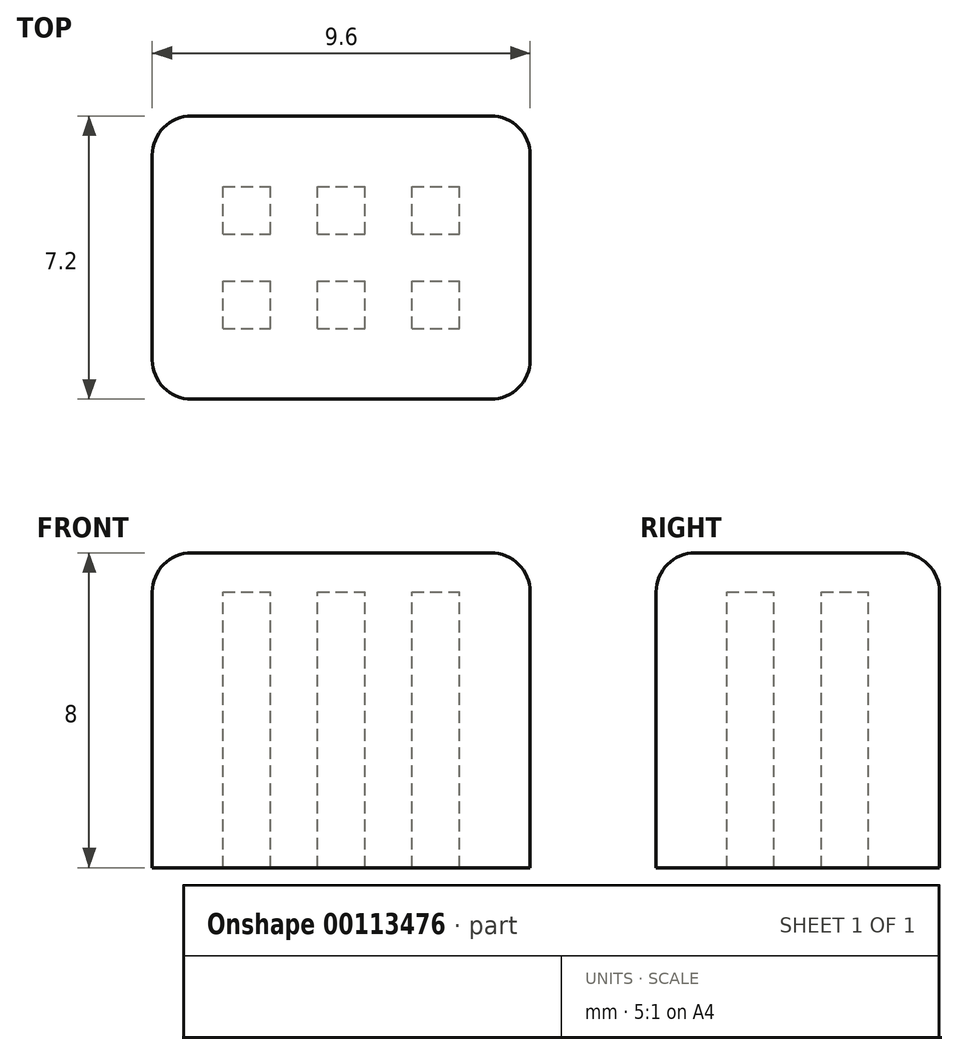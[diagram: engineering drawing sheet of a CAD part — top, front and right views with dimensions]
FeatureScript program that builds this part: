
annotation { "Feature Type Name" : "Feature", "Feature Type Description" : "" }
export const myFeature = defineFeature(function(context is Context, id is Id, definition is map)
    precondition{}
    {
        {
            var Q0;
            Q0=qCreatedBy(makeId("Top.planeOp"),FACE);
            var sketch = newSketch(context, id + "F0", { "sketchPlane" : qUnion([Q0])});
            skLineSegment(sketch, "E0.bottom", {"start": v(0, 0) * mm, "end": v(2.4, 0) * mm});
            skLineSegment(sketch, "E0.top", {"start": v(0, 2.4) * mm, "end": v(2.4, 2.4) * mm});
            skLineSegment(sketch, "E0.left", {"start": v(0, 0) * mm, "end": v(0, 2.4) * mm});
            skLineSegment(sketch, "E0.right", {"start": v(2.4, 0) * mm, "end": v(2.4, 2.4) * mm});
            skLineSegment(sketch, "E1.bottom", {"start": v(0.6, 0.6) * mm, "end": v(1.8, 0.6) * mm});
            skLineSegment(sketch, "E1.top", {"start": v(0.6, 1.8) * mm, "end": v(1.8, 1.8) * mm});
            skLineSegment(sketch, "E1.left", {"start": v(0.6, 0.6) * mm, "end": v(0.6, 1.8) * mm});
            skLineSegment(sketch, "E1.right", {"start": v(1.8, 0.6) * mm, "end": v(1.8, 1.8) * mm});
            skLineSegment(sketch, "E2", {"start": v(1.2, 1.8) * mm, "end": v(1.2, 2.4) * mm, "construction": true});
            skLineSegment(sketch, "E3", {"start": v(0, 1.2) * mm, "end": v(0.6, 1.2) * mm, "construction": true});
            skLineSegment(sketch, "E4.0.1.0", {"start": v(0, 3.6) * mm, "end": v(0.6, 3.6) * mm, "construction": true});
            skLineSegment(sketch, "E4.0.1.1", {"start": v(0, 4.8) * mm, "end": v(2.4, 4.8) * mm});
            skLineSegment(sketch, "E4.0.1.2", {"start": v(2.4, 2.4) * mm, "end": v(2.4, 4.8) * mm});
            skLineSegment(sketch, "E4.0.1.3", {"start": v(1.8, 3) * mm, "end": v(1.8, 4.2) * mm});
            skLineSegment(sketch, "E4.0.1.4", {"start": v(1.2, 4.2) * mm, "end": v(1.2, 4.8) * mm, "construction": true});
            skLineSegment(sketch, "E4.0.1.5", {"start": v(0, 2.4) * mm, "end": v(0, 4.8) * mm});
            skLineSegment(sketch, "E4.0.1.6", {"start": v(0.6, 3) * mm, "end": v(1.8, 3) * mm});
            skLineSegment(sketch, "E4.0.1.7", {"start": v(0.6, 3) * mm, "end": v(0.6, 4.2) * mm});
            skLineSegment(sketch, "E4.0.1.8", {"start": v(0.6, 4.2) * mm, "end": v(1.8, 4.2) * mm});
            skLineSegment(sketch, "E4.1.0.0", {"start": v(2.4, 1.2) * mm, "end": v(3, 1.2) * mm, "construction": true});
            skLineSegment(sketch, "E4.1.0.1", {"start": v(2.4, 2.4) * mm, "end": v(4.8, 2.4) * mm});
            skLineSegment(sketch, "E4.1.0.2", {"start": v(4.8, 0) * mm, "end": v(4.8, 2.4) * mm});
            skLineSegment(sketch, "E4.1.0.3", {"start": v(4.2, 0.6) * mm, "end": v(4.2, 1.8) * mm});
            skLineSegment(sketch, "E4.1.0.4", {"start": v(3.6, 1.8) * mm, "end": v(3.6, 2.4) * mm, "construction": true});
            skLineSegment(sketch, "E4.1.0.6", {"start": v(3, 0.6) * mm, "end": v(4.2, 0.6) * mm});
            skLineSegment(sketch, "E4.1.0.7", {"start": v(3, 0.6) * mm, "end": v(3, 1.8) * mm});
            skLineSegment(sketch, "E4.1.0.8", {"start": v(3, 1.8) * mm, "end": v(4.2, 1.8) * mm});
            skLineSegment(sketch, "E4.1.0.9", {"start": v(2.4, 0) * mm, "end": v(4.8, 0) * mm});
            skLineSegment(sketch, "E4.1.1.0", {"start": v(2.4, 3.6) * mm, "end": v(3, 3.6) * mm, "construction": true});
            skLineSegment(sketch, "E4.1.1.1", {"start": v(2.4, 4.8) * mm, "end": v(4.8, 4.8) * mm});
            skLineSegment(sketch, "E4.1.1.2", {"start": v(4.8, 2.4) * mm, "end": v(4.8, 4.8) * mm});
            skLineSegment(sketch, "E4.1.1.3", {"start": v(4.2, 3) * mm, "end": v(4.2, 4.2) * mm});
            skLineSegment(sketch, "E4.1.1.4", {"start": v(3.6, 4.2) * mm, "end": v(3.6, 4.8) * mm, "construction": true});
            skLineSegment(sketch, "E4.1.1.5", {"start": v(2.4, 2.4) * mm, "end": v(2.4, 4.8) * mm});
            skLineSegment(sketch, "E4.1.1.6", {"start": v(3, 3) * mm, "end": v(4.2, 3) * mm});
            skLineSegment(sketch, "E4.1.1.7", {"start": v(3, 3) * mm, "end": v(3, 4.2) * mm});
            skLineSegment(sketch, "E4.1.1.8", {"start": v(3, 4.2) * mm, "end": v(4.2, 4.2) * mm});
            skLineSegment(sketch, "E4.1.1.9", {"start": v(2.4, 2.4) * mm, "end": v(4.8, 2.4) * mm});
            skLineSegment(sketch, "E4.2.0.0", {"start": v(4.8, 1.2) * mm, "end": v(5.4, 1.2) * mm, "construction": true});
            skLineSegment(sketch, "E4.2.0.1", {"start": v(4.8, 2.4) * mm, "end": v(7.2, 2.4) * mm});
            skLineSegment(sketch, "E4.2.0.2", {"start": v(7.2, 0) * mm, "end": v(7.2, 2.4) * mm});
            skLineSegment(sketch, "E4.2.0.3", {"start": v(6.6, 0.6) * mm, "end": v(6.6, 1.8) * mm});
            skLineSegment(sketch, "E4.2.0.4", {"start": v(6, 1.8) * mm, "end": v(6, 2.4) * mm, "construction": true});
            skLineSegment(sketch, "E4.2.0.5", {"start": v(4.8, 0) * mm, "end": v(4.8, 2.4) * mm});
            skLineSegment(sketch, "E4.2.0.6", {"start": v(5.4, 0.6) * mm, "end": v(6.6, 0.6) * mm});
            skLineSegment(sketch, "E4.2.0.7", {"start": v(5.4, 0.6) * mm, "end": v(5.4, 1.8) * mm});
            skLineSegment(sketch, "E4.2.0.8", {"start": v(5.4, 1.8) * mm, "end": v(6.6, 1.8) * mm});
            skLineSegment(sketch, "E4.2.0.9", {"start": v(4.8, 0) * mm, "end": v(7.2, 0) * mm});
            skLineSegment(sketch, "E4.2.1.0", {"start": v(4.8, 3.6) * mm, "end": v(5.4, 3.6) * mm, "construction": true});
            skLineSegment(sketch, "E4.2.1.1", {"start": v(4.8, 4.8) * mm, "end": v(7.2, 4.8) * mm});
            skLineSegment(sketch, "E4.2.1.2", {"start": v(7.2, 2.4) * mm, "end": v(7.2, 4.8) * mm});
            skLineSegment(sketch, "E4.2.1.3", {"start": v(6.6, 3) * mm, "end": v(6.6, 4.2) * mm});
            skLineSegment(sketch, "E4.2.1.4", {"start": v(6, 4.2) * mm, "end": v(6, 4.8) * mm, "construction": true});
            skLineSegment(sketch, "E4.2.1.5", {"start": v(4.8, 2.4) * mm, "end": v(4.8, 4.8) * mm});
            skLineSegment(sketch, "E4.2.1.6", {"start": v(5.4, 3) * mm, "end": v(6.6, 3) * mm});
            skLineSegment(sketch, "E4.2.1.7", {"start": v(5.4, 3) * mm, "end": v(5.4, 4.2) * mm});
            skLineSegment(sketch, "E4.2.1.8", {"start": v(5.4, 4.2) * mm, "end": v(6.6, 4.2) * mm});
            skLineSegment(sketch, "E4.2.1.9", {"start": v(4.8, 2.4) * mm, "end": v(7.2, 2.4) * mm});
            skLineSegment(sketch, "E4.direction1", {"start": v(0, 0) * mm, "end": v(2.4, 0) * mm, "construction": true});
            skLineSegment(sketch, "E4.direction2", {"start": v(0, 0) * mm, "end": v(0, 2.4) * mm, "construction": true});
            skLineSegment(sketch, "E5.0", {"start": v(-1.2, 2.4) * mm, "end": v(-1.2, 6) * mm});
            skLineSegment(sketch, "E5.1", {"start": v(-1.2, -1.2) * mm, "end": v(-1.2, 2.4) * mm});
            skLineSegment(sketch, "E5.2", {"start": v(-1.2, 6) * mm, "end": v(2.4, 6) * mm});
            skLineSegment(sketch, "E5.3", {"start": v(-1.2, -1.2) * mm, "end": v(2.4, -1.2) * mm});
            skLineSegment(sketch, "E5.4", {"start": v(2.4, -1.2) * mm, "end": v(4.8, -1.2) * mm});
            skLineSegment(sketch, "E5.5", {"start": v(4.8, -1.2) * mm, "end": v(8.4, -1.2) * mm});
            skLineSegment(sketch, "E5.6", {"start": v(2.4, 6) * mm, "end": v(4.8, 6) * mm});
            skLineSegment(sketch, "E5.7", {"start": v(4.8, 6) * mm, "end": v(8.4, 6) * mm});
            skLineSegment(sketch, "E5.8", {"start": v(8.4, 2.4) * mm, "end": v(8.4, 6) * mm});
            skLineSegment(sketch, "E5.9", {"start": v(8.4, -1.2) * mm, "end": v(8.4, 2.4) * mm});
            skSolve(sketch);
        }
        {
            var Q0;
            Q0 = qSketchRegion(id + "F0", true);
            var Q1;
            Q1=makeQuery(id+"F0.imprint","IMPRINT",FACE,{"disambiguationData":[TD([[makeQuery(id+"F0.imprint","IMPRINT",EDGE,{"derivedFrom":sQuery(id+"F0.wireOp",EDGE,"b262808e-0304-4559-aea2-205f56d76e43.0.1.0")}),-1.0]])]});
            var Q2;
            {var subQ0=sQuery(id+"F0.wireOp",EDGE,"rw9Zj4h6-CSxw-FYrh-HEQo-mKNTmKfgoEyw.bottom");Q2=makeQuery(id+"F0.imprint","IMPRINT",FACE,{"disambiguationData":[TD([[makeQuery(id+"F0.imprint","IMPRINT",EDGE,{"derivedFrom":subQ0}),1.0]])]});}
            var Q3;
            Q3=makeQuery(id+"F0.imprint","IMPRINT",FACE,{"disambiguationData":[TD([[makeQuery(id+"F0.imprint","IMPRINT",EDGE,{"derivedFrom":sQuery(id+"F0.wireOp",EDGE,"b262808e-0304-4559-aea2-205f56d76e43.1.0.1")}),1.0]])]});
            var Q4;
            Q4=makeQuery(id+"F0.imprint","IMPRINT",FACE,{"disambiguationData":[TD([[makeQuery(id+"F0.imprint","IMPRINT",EDGE,{"derivedFrom":sQuery(id+"F0.wireOp",EDGE,"b262808e-0304-4559-aea2-205f56d76e43.2.1.0")}),-1.0]])]});
            var Q5;
            Q5=makeQuery(id+"F0.imprint","IMPRINT",FACE,{"disambiguationData":[TD([[makeQuery(id+"F0.imprint","IMPRINT",EDGE,{"derivedFrom":sQuery(id+"F0.wireOp",EDGE,"b262808e-0304-4559-aea2-205f56d76e43.1.1.0")}),-1.0]])]});
            var Q6;
            Q6=makeQuery(id+"F0.imprint","IMPRINT",FACE,{"disambiguationData":[TD([[makeQuery(id+"F0.imprint","IMPRINT",EDGE,{"derivedFrom":sQuery(id+"F0.wireOp",EDGE,"b262808e-0304-4559-aea2-205f56d76e43.2.0.1")}),1.0]])]});
            var Q7;
            Q7=makeQuery(id+"F0.imprint","IMPRINT",FACE,{"disambiguationData":[TD([[makeQuery(id+"F0.imprint","IMPRINT",EDGE,{"derivedFrom":sQuery(id+"F0.wireOp",EDGE,"E4.0.1.1")}),-1.0]])]});
            var Q8;
            Q8=makeQuery(id+"F0.imprint","IMPRINT",FACE,{"disambiguationData":[TD([[makeQuery(id+"F0.imprint","IMPRINT",EDGE,{"derivedFrom":sQuery(id+"F0.wireOp",EDGE,"E4.1.1.1")}),-1.0]])]});
            var Q9;
            Q9=makeQuery(id+"F0.imprint","IMPRINT",FACE,{"disambiguationData":[TD([[makeQuery(id+"F0.imprint","IMPRINT",EDGE,{"derivedFrom":sQuery(id+"F0.wireOp",EDGE,"E4.2.1.1")}),-1.0]])]});
            var Q10;
            Q10=makeQuery(id+"F0.imprint","IMPRINT",FACE,{"disambiguationData":[TD([[makeQuery(id+"F0.imprint","IMPRINT",EDGE,{"derivedFrom":sQuery(id+"F0.wireOp",EDGE,"E4.2.0.2")}),1.0]])]});
            var Q11;
            Q11=makeQuery(id+"F0.imprint","IMPRINT",FACE,{"disambiguationData":[TD([[makeQuery(id+"F0.imprint","IMPRINT",EDGE,{"derivedFrom":sQuery(id+"F0.wireOp",EDGE,"E4.1.0.3")}),-1.0]])]});
            var Q12;
            Q12=makeQuery(id+"F0.imprint","IMPRINT",FACE,{"disambiguationData":[TD([[makeQuery(id+"F0.imprint","IMPRINT",EDGE,{"derivedFrom":sQuery(id+"F0.wireOp",EDGE,"E0.bottom")}),1.0]])]});
            extrude(context, id + "F1", {"entities" : qUnion([Q0, Q1, Q2, Q3, Q4, Q5, Q6, Q7, Q8, Q9, Q10, Q11, Q12]), "oppositeDirection" : true, "depth" : 7 * mm});
        }
        {
            var Q0;
            Q0=makeQuery(id+"F0.imprint","IMPRINT",FACE,{"disambiguationData":[TD([[makeQuery(id+"F0.imprint","IMPRINT",EDGE,{"derivedFrom":sQuery(id+"F0.wireOp",EDGE,"rw9Zj4h6-CSxw-FYrh-HEQo-mKNTmKfgoEyw.bottom")}),1.0]])]});
            var Q1;
            Q1=makeQuery(id+"F0.imprint","IMPRINT",FACE,{"disambiguationData":[TD([[makeQuery(id+"F0.imprint","IMPRINT",EDGE,{"derivedFrom":sQuery(id+"F0.wireOp",EDGE,"JQ0vZeJZ-ZWkE-5OqH-aotH-A3nAdsIy9p33.bottom")}),1.0]])]});
            var Q2;
            {var subQ0=sQuery(id+"F0.wireOp",EDGE,"rw9Zj4h6-CSxw-FYrh-HEQo-mKNTmKfgoEyw.bottom");Q2=makeQuery(id+"F0.imprint","IMPRINT",FACE,{"disambiguationData":[TD([[makeQuery(id+"F0.imprint","IMPRINT",EDGE,{"derivedFrom":subQ0}),-1.0]])]});}
            var Q3;
            Q3=makeQuery(id+"F0.imprint","IMPRINT",FACE,{"disambiguationData":[TD([[makeQuery(id+"F0.imprint","IMPRINT",EDGE,{"derivedFrom":sQuery(id+"F0.wireOp",EDGE,"b262808e-0304-4559-aea2-205f56d76e43.0.1.0")}),-1.0]])]});
            var Q4;
            Q4=makeQuery(id+"F0.imprint","IMPRINT",FACE,{"disambiguationData":[TD([[makeQuery(id+"F0.imprint","IMPRINT",EDGE,{"derivedFrom":sQuery(id+"F0.wireOp",EDGE,"b262808e-0304-4559-aea2-205f56d76e43.0.1.1")}),-1.0]])]});
            var Q5;
            Q5=makeQuery(id+"F0.imprint","IMPRINT",FACE,{"disambiguationData":[TD([[makeQuery(id+"F0.imprint","IMPRINT",EDGE,{"derivedFrom":sQuery(id+"F0.wireOp",EDGE,"b262808e-0304-4559-aea2-205f56d76e43.1.1.1")}),-1.0]])]});
            var Q6;
            Q6=makeQuery(id+"F0.imprint","IMPRINT",FACE,{"disambiguationData":[TD([[makeQuery(id+"F0.imprint","IMPRINT",EDGE,{"derivedFrom":sQuery(id+"F0.wireOp",EDGE,"b262808e-0304-4559-aea2-205f56d76e43.1.1.0")}),-1.0]])]});
            var Q7;
            Q7=makeQuery(id+"F0.imprint","IMPRINT",FACE,{"disambiguationData":[TD([[makeQuery(id+"F0.imprint","IMPRINT",EDGE,{"derivedFrom":sQuery(id+"F0.wireOp",EDGE,"JQ0vZeJZ-ZWkE-5OqH-aotH-A3nAdsIy9p33.top")}),-1.0]])]});
            var Q8;
            Q8=makeQuery(id+"F0.imprint","IMPRINT",FACE,{"disambiguationData":[TD([[makeQuery(id+"F0.imprint","IMPRINT",EDGE,{"derivedFrom":sQuery(id+"F0.wireOp",EDGE,"b262808e-0304-4559-aea2-205f56d76e43.1.0.1")}),-1.0]])]});
            var Q9;
            Q9=makeQuery(id+"F0.imprint","IMPRINT",FACE,{"disambiguationData":[TD([[makeQuery(id+"F0.imprint","IMPRINT",EDGE,{"derivedFrom":sQuery(id+"F0.wireOp",EDGE,"b262808e-0304-4559-aea2-205f56d76e43.2.0.1")}),-1.0]])]});
            var Q10;
            Q10=makeQuery(id+"F0.imprint","IMPRINT",FACE,{"disambiguationData":[TD([[makeQuery(id+"F0.imprint","IMPRINT",EDGE,{"derivedFrom":sQuery(id+"F0.wireOp",EDGE,"b262808e-0304-4559-aea2-205f56d76e43.2.1.1")}),-1.0]])]});
            var Q11;
            Q11=makeQuery(id+"F0.imprint","IMPRINT",FACE,{"disambiguationData":[TD([[makeQuery(id+"F0.imprint","IMPRINT",EDGE,{"derivedFrom":sQuery(id+"F0.wireOp",EDGE,"b262808e-0304-4559-aea2-205f56d76e43.2.1.0")}),-1.0]])]});
            var Q12;
            Q12=makeQuery(id+"F0.imprint","IMPRINT",FACE,{"disambiguationData":[TD([[makeQuery(id+"F0.imprint","IMPRINT",EDGE,{"derivedFrom":sQuery(id+"F0.wireOp",EDGE,"b262808e-0304-4559-aea2-205f56d76e43.2.0.1")}),1.0]])]});
            var Q13;
            Q13=makeQuery(id+"F0.imprint","IMPRINT",FACE,{"disambiguationData":[TD([[makeQuery(id+"F0.imprint","IMPRINT",EDGE,{"derivedFrom":sQuery(id+"F0.wireOp",EDGE,"b262808e-0304-4559-aea2-205f56d76e43.1.0.1")}),1.0]])]});
            var Q14;
            Q14=makeQuery(id+"F0.imprint","IMPRINT",FACE,{"disambiguationData":[TD([[makeQuery(id+"F0.imprint","IMPRINT",EDGE,{"derivedFrom":sQuery(id+"F0.wireOp",EDGE,"E0.bottom")}),-1.0]])]});
            var Q15;
            Q15=makeQuery(id+"F0.imprint","IMPRINT",FACE,{"disambiguationData":[TD([[makeQuery(id+"F0.imprint","IMPRINT",EDGE,{"derivedFrom":sQuery(id+"F0.wireOp",EDGE,"E4.1.1.1")}),-1.0]])]});
            var Q16;
            Q16=makeQuery(id+"F0.imprint","IMPRINT",FACE,{"disambiguationData":[TD([[makeQuery(id+"F0.imprint","IMPRINT",EDGE,{"derivedFrom":sQuery(id+"F0.wireOp",EDGE,"E4.2.1.3")}),1.0]])]});
            var Q17;
            Q17=makeQuery(id+"F0.imprint","IMPRINT",FACE,{"disambiguationData":[TD([[makeQuery(id+"F0.imprint","IMPRINT",EDGE,{"derivedFrom":sQuery(id+"F0.wireOp",EDGE,"E4.2.1.1")}),-1.0]])]});
            var Q18;
            Q18=makeQuery(id+"F0.imprint","IMPRINT",FACE,{"disambiguationData":[TD([[makeQuery(id+"F0.imprint","IMPRINT",EDGE,{"derivedFrom":sQuery(id+"F0.wireOp",EDGE,"E4.1.1.3")}),1.0]])]});
            var Q19;
            Q19=makeQuery(id+"F0.imprint","IMPRINT",FACE,{"disambiguationData":[TD([[makeQuery(id+"F0.imprint","IMPRINT",EDGE,{"derivedFrom":sQuery(id+"F0.wireOp",EDGE,"E4.0.1.3")}),1.0]])]});
            var Q20;
            Q20=makeQuery(id+"F0.imprint","IMPRINT",FACE,{"disambiguationData":[TD([[makeQuery(id+"F0.imprint","IMPRINT",EDGE,{"derivedFrom":sQuery(id+"F0.wireOp",EDGE,"E4.0.1.1")}),-1.0]])]});
            var Q21;
            Q21=makeQuery(id+"F0.imprint","IMPRINT",FACE,{"disambiguationData":[TD([[makeQuery(id+"F0.imprint","IMPRINT",EDGE,{"derivedFrom":sQuery(id+"F0.wireOp",EDGE,"E0.bottom")}),1.0]])]});
            var Q22;
            Q22=makeQuery(id+"F0.imprint","IMPRINT",FACE,{"disambiguationData":[TD([[makeQuery(id+"F0.imprint","IMPRINT",EDGE,{"derivedFrom":sQuery(id+"F0.wireOp",EDGE,"E1.bottom")}),1.0]])]});
            var Q23;
            Q23=makeQuery(id+"F0.imprint","IMPRINT",FACE,{"disambiguationData":[TD([[makeQuery(id+"F0.imprint","IMPRINT",EDGE,{"derivedFrom":sQuery(id+"F0.wireOp",EDGE,"E4.1.0.3")}),1.0]])]});
            var Q24;
            Q24=makeQuery(id+"F0.imprint","IMPRINT",FACE,{"disambiguationData":[TD([[makeQuery(id+"F0.imprint","IMPRINT",EDGE,{"derivedFrom":sQuery(id+"F0.wireOp",EDGE,"E4.1.0.3")}),-1.0]])]});
            var Q25;
            Q25=makeQuery(id+"F0.imprint","IMPRINT",FACE,{"disambiguationData":[TD([[makeQuery(id+"F0.imprint","IMPRINT",EDGE,{"derivedFrom":sQuery(id+"F0.wireOp",EDGE,"E4.2.0.3")}),1.0]])]});
            var Q26;
            Q26=makeQuery(id+"F0.imprint","IMPRINT",FACE,{"disambiguationData":[TD([[makeQuery(id+"F0.imprint","IMPRINT",EDGE,{"derivedFrom":sQuery(id+"F0.wireOp",EDGE,"E4.2.0.2")}),1.0]])]});
            extrude(context, id + "F2", {"entities" : qUnion([Q0, Q1, Q2, Q3, Q4, Q5, Q6, Q7, Q8, Q9, Q10, Q11, Q12, Q13, Q14, Q15, Q16, Q17, Q18, Q19, Q20, Q21, Q22, Q23, Q24, Q25, Q26]), "operationType" : NewBodyOperationType.ADD, "depth" : 1 * mm});
        }
        {
            var Q0;
            {var subQ0=sQuery(id+"F0.wireOp",EDGE,"x7mGPeTP-9ZWt-URV3-VnWX-TF2VCcUrg2Dr.left");var subQ1=sQuery(id+"F0.wireOp",EDGE,"x7mGPeTP-9ZWt-URV3-VnWX-TF2VCcUrg2Dr.top");Q0=makeQuery(id+"F2.boolean.opBoolean","MERGE",EDGE,{"derivedFrom":[makeQuery(id+"F1.opExtrude","SWEPT_EDGE",EDGE,{"disambiguationData":[OSD([subQ1,subQ0])]}),makeQuery(id+"F2.opExtrude","SWEPT_EDGE",EDGE,{"disambiguationData":[OSD([subQ1,subQ0])]})]});}
            var Q1;
            {var subQ0=sQuery(id+"F0.wireOp",EDGE,"x7mGPeTP-9ZWt-URV3-VnWX-TF2VCcUrg2Dr.left");var subQ1=sQuery(id+"F0.wireOp",EDGE,"x7mGPeTP-9ZWt-URV3-VnWX-TF2VCcUrg2Dr.bottom");Q1=makeQuery(id+"F2.boolean.opBoolean","MERGE",EDGE,{"derivedFrom":[makeQuery(id+"F1.opExtrude","SWEPT_EDGE",EDGE,{"disambiguationData":[OSD([subQ1,subQ0])]}),makeQuery(id+"F2.opExtrude","SWEPT_EDGE",EDGE,{"disambiguationData":[OSD([subQ1,subQ0])]})]});}
            var Q2;
            Q2=makeQuery(id+"F2.opExtrude","CAP_EDGE",EDGE,{"disambiguationData":[OSD([sQuery(id+"F0.wireOp",EDGE,"x7mGPeTP-9ZWt-URV3-VnWX-TF2VCcUrg2Dr.top")])],"isStart":false});
            var Q3;
            Q3=makeQuery(id+"F2.opExtrude","CAP_EDGE",EDGE,{"disambiguationData":[OSD([sQuery(id+"F0.wireOp",EDGE,"x7mGPeTP-9ZWt-URV3-VnWX-TF2VCcUrg2Dr.left")])],"isStart":false});
            var Q4;
            Q4=makeQuery(id+"F2.opExtrude","CAP_EDGE",EDGE,{"disambiguationData":[OSD([sQuery(id+"F0.wireOp",EDGE,"x7mGPeTP-9ZWt-URV3-VnWX-TF2VCcUrg2Dr.bottom")])],"isStart":false});
            var Q5;
            Q5=makeQuery(id+"F2.opExtrude","CAP_EDGE",EDGE,{"disambiguationData":[OSD([sQuery(id+"F0.wireOp",EDGE,"x7mGPeTP-9ZWt-URV3-VnWX-TF2VCcUrg2Dr.right")])],"isStart":false});
            var Q6;
            {var subQ0=sQuery(id+"F0.wireOp",EDGE,"x7mGPeTP-9ZWt-URV3-VnWX-TF2VCcUrg2Dr.right");var subQ1=sQuery(id+"F0.wireOp",EDGE,"x7mGPeTP-9ZWt-URV3-VnWX-TF2VCcUrg2Dr.top");Q6=makeQuery(id+"F2.boolean.opBoolean","MERGE",EDGE,{"derivedFrom":[makeQuery(id+"F1.opExtrude","SWEPT_EDGE",EDGE,{"disambiguationData":[OSD([subQ1,subQ0])]}),makeQuery(id+"F2.opExtrude","SWEPT_EDGE",EDGE,{"disambiguationData":[OSD([subQ1,subQ0])]})]});}
            var Q7;
            {var subQ0=sQuery(id+"F0.wireOp",EDGE,"x7mGPeTP-9ZWt-URV3-VnWX-TF2VCcUrg2Dr.right");var subQ1=sQuery(id+"F0.wireOp",EDGE,"x7mGPeTP-9ZWt-URV3-VnWX-TF2VCcUrg2Dr.bottom");Q7=makeQuery(id+"F2.boolean.opBoolean","MERGE",EDGE,{"derivedFrom":[makeQuery(id+"F1.opExtrude","SWEPT_EDGE",EDGE,{"disambiguationData":[OSD([subQ1,subQ0])]}),makeQuery(id+"F2.opExtrude","SWEPT_EDGE",EDGE,{"disambiguationData":[OSD([subQ1,subQ0])]})]});}
            var Q8;
            {var subQ0=sQuery(id+"F0.wireOp",EDGE,"E5.3");var subQ1=sQuery(id+"F0.wireOp",EDGE,"E5.1");Q8=makeQuery(id+"F2.boolean.opBoolean","MERGE",EDGE,{"derivedFrom":[makeQuery(id+"F1.opExtrude","SWEPT_EDGE",EDGE,{"disambiguationData":[OSD([subQ1,subQ0])]}),makeQuery(id+"F2.opExtrude","SWEPT_EDGE",EDGE,{"disambiguationData":[OSD([subQ1,subQ0])]})]});}
            var Q9;
            Q9=makeQuery(id+"F2.opExtrude","CAP_EDGE",EDGE,{"disambiguationData":[OSD([sQuery(id+"F0.wireOp",EDGE,"E5.0"),sQuery(id+"F0.wireOp",EDGE,"E5.1")])],"isStart":false});
            var Q10;
            Q10=makeQuery(id+"F2.opExtrude","CAP_EDGE",EDGE,{"disambiguationData":[OSD([sQuery(id+"F0.wireOp",EDGE,"E5.3"),sQuery(id+"F0.wireOp",EDGE,"E5.4"),sQuery(id+"F0.wireOp",EDGE,"E5.5")])],"isStart":false});
            var Q11;
            {var subQ0=sQuery(id+"F0.wireOp",EDGE,"E5.9");var subQ1=sQuery(id+"F0.wireOp",EDGE,"E5.5");Q11=makeQuery(id+"F2.boolean.opBoolean","MERGE",EDGE,{"derivedFrom":[makeQuery(id+"F1.opExtrude","SWEPT_EDGE",EDGE,{"disambiguationData":[OSD([subQ1,subQ0])]}),makeQuery(id+"F2.opExtrude","SWEPT_EDGE",EDGE,{"disambiguationData":[OSD([subQ1,subQ0])]})]});}
            var Q12;
            Q12=makeQuery(id+"F2.opExtrude","CAP_EDGE",EDGE,{"disambiguationData":[OSD([sQuery(id+"F0.wireOp",EDGE,"E5.8"),sQuery(id+"F0.wireOp",EDGE,"E5.9")])],"isStart":false});
            var Q13;
            Q13=makeQuery(id+"F2.opExtrude","CAP_EDGE",EDGE,{"disambiguationData":[OSD([sQuery(id+"F0.wireOp",EDGE,"E5.2"),sQuery(id+"F0.wireOp",EDGE,"E5.6"),sQuery(id+"F0.wireOp",EDGE,"E5.7")])],"isStart":false});
            var Q14;
            {var subQ0=sQuery(id+"F0.wireOp",EDGE,"E5.8");var subQ1=sQuery(id+"F0.wireOp",EDGE,"E5.7");Q14=makeQuery(id+"F2.boolean.opBoolean","MERGE",EDGE,{"derivedFrom":[makeQuery(id+"F1.opExtrude","SWEPT_EDGE",EDGE,{"disambiguationData":[OSD([subQ1,subQ0])]}),makeQuery(id+"F2.opExtrude","SWEPT_EDGE",EDGE,{"disambiguationData":[OSD([subQ1,subQ0])]})]});}
            var Q15;
            {var subQ0=sQuery(id+"F0.wireOp",EDGE,"E5.2");var subQ1=sQuery(id+"F0.wireOp",EDGE,"E5.0");Q15=makeQuery(id+"F2.boolean.opBoolean","MERGE",EDGE,{"derivedFrom":[makeQuery(id+"F1.opExtrude","SWEPT_EDGE",EDGE,{"disambiguationData":[OSD([subQ1,subQ0])]}),makeQuery(id+"F2.opExtrude","SWEPT_EDGE",EDGE,{"disambiguationData":[OSD([subQ1,subQ0])]})]});}
            fillet(context, id + "F3", {"entities" : qUnion([Q0, Q1, Q2, Q3, Q4, Q5, Q6, Q7, Q8, Q9, Q10, Q11, Q12, Q13, Q14, Q15]), "radius" : 1 * mm, "tangentPropagation" : true, "allowEdgeOverflow" : false});
        }
    });
